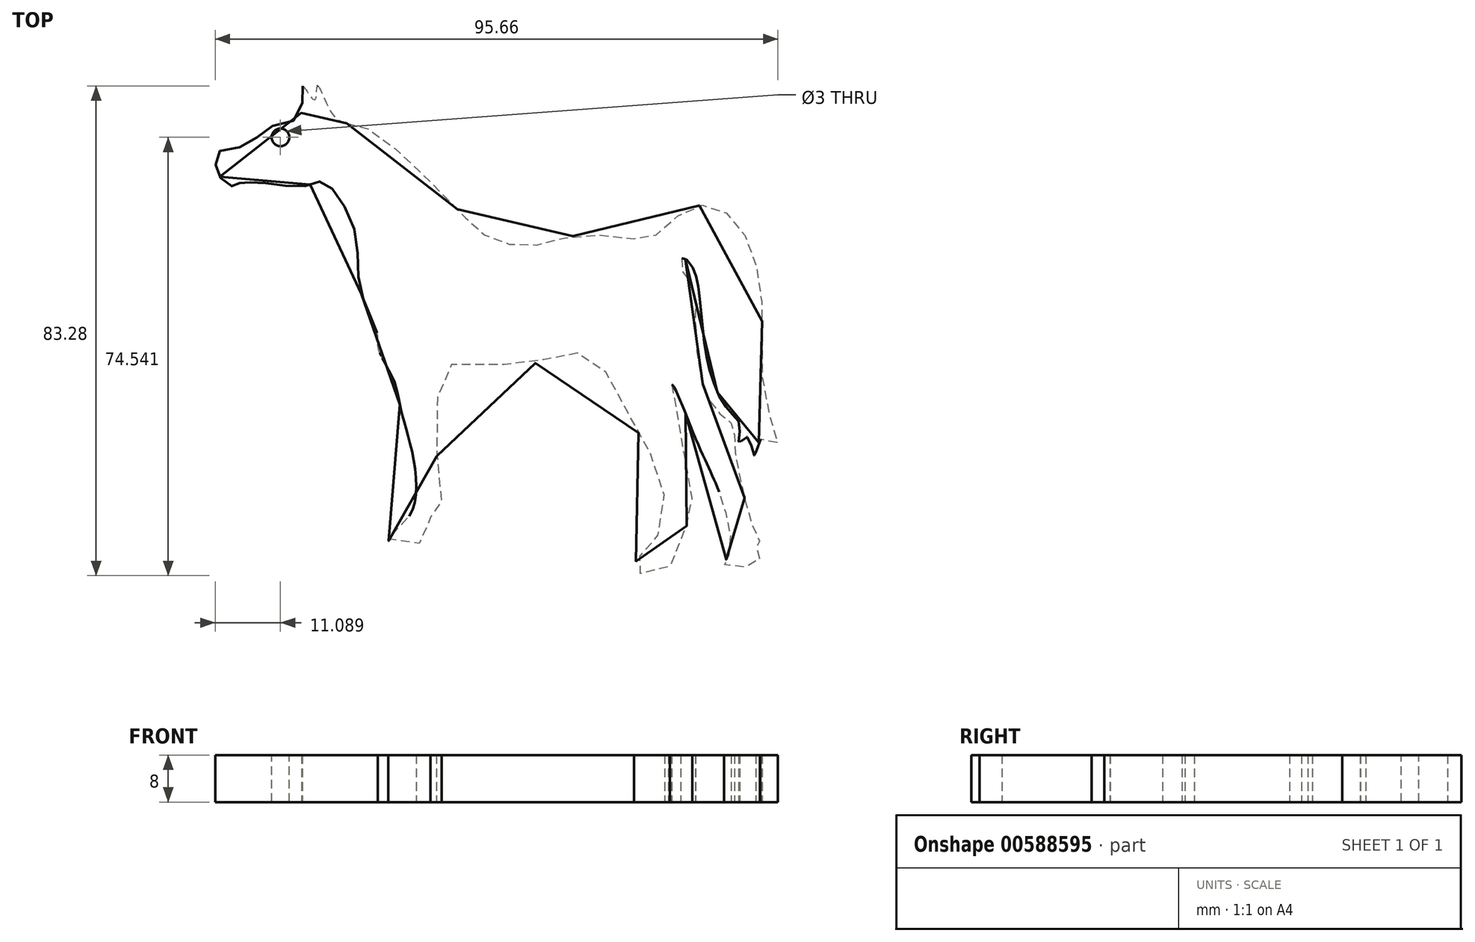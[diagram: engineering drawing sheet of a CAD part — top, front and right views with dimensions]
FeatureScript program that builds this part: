
annotation { "Feature Type Name" : "Feature", "Feature Type Description" : "" }
export const myFeature = defineFeature(function(context is Context, id is Id, definition is map)
    precondition{}
    {
        {
            var Q0;
            Q0=qCreatedBy(makeId("Top.planeOp"),FACE);
            var sketch = newSketch(context, id + "F0", { "sketchPlane" : qUnion([Q0])});
            skFitSpline(sketch, "E0", {"points": [v(-73.14, 76.23) * mm, v(-69.83, 75.44) * mm, v(-63.8, 70.88) * mm, v(-58.9, 66.2) * mm, v(-53.2, 60.4) * mm, v(-49.66, 57.2) * mm, v(-45.1, 55.6) * mm, v(-39.86, 55.72) * mm, v(-33.59, 57.2) * mm, v(-24.7, 56.63) * mm, v(-21.05, 56.97) * mm, v(-16.83, 60.5) * mm, v(-12.27, 62.33) * mm, v(-8.06, 60.5) * mm, v(-4.52, 55.15) * mm, v(-2.7, 46.94) * mm, v(-2.59, 37.03) * mm, v(-1.56, 27.45) * mm, v(0, 21.87) * mm, v(-2.47, 22.78) * mm, v(-3.84, 19.7) * mm, v(-5.1, 22.9) * mm, v(-6.46, 21.87) * mm, v(-6.35, 24.83) * mm, v(-8.29, 27.45) * mm, v(-11.25, 33.5) * mm, v(-12.62, 41.02) * mm, v(-13.41, 48.65) * mm, v(-14.67, 52.19) * mm, v(-16.15, 53.33) * mm, v(-15.92, 50.7) * mm, v(-14.33, 48.54) * mm, v(-13.87, 41.81) * mm, v(-12.39, 31.1) * mm, v(-9.65, 26.77) * mm, v(-7.49, 24.83) * mm, v(-7.26, 21.98) * mm, v(-6.12, 15.14) * mm, v(-3.73, 6.7) * mm, v(-2.93, 4.43) * mm, v(-3.61, 3.97) * mm, v(-3.04, 1.58) * mm, v(-8.86, 1.12) * mm, v(-8.29, 2.6) * mm, v(-8.17, 7.96) * mm, v(-10.45, 15.03) * mm, v(-13.76, 22.44) * mm, v(-17.86, 31.78) * mm, v(-15.24, 17.54) * mm, v(-14.9, 8.08) * mm, v(-15.8, 7.4) * mm, v(-16.26, 4.77) * mm, v(-18.43, 3.3) * mm, v(-18.43, 0) * mm, v(-23.9, 0) * mm, v(-24.13, 1.47) * mm, v(-22.42, 3.52) * mm, v(-20.02, 6.6) * mm, v(-19.45, 14.92) * mm, v(-23.33, 23.24) * mm, v(-28.23, 32.47) * mm, v(-32.33, 36.8) * mm, v(-38.37, 36.57) * mm, v(-43.05, 35.09) * mm, v(-55.59, 35.09) * mm, v(-57.75, 29.28) * mm, v(-57.52, 15.49) * mm, v(-57.4, 9.9) * mm, v(-58.78, 9.45) * mm, v(-59.46, 5.57) * mm, v(-65.84, 5) * mm, v(-65.73, 6.14) * mm, v(-62.08, 10.24) * mm, v(-62.08, 20.5) * mm, v(-64.02, 27.8) * mm, v(-65.16, 32.47) * mm, v(-67.78, 37.94) * mm, v(-67.9, 40.1) * mm, v(-69.03, 43.18) * mm, v(-71.09, 49.1) * mm, v(-71.54, 56.74) * mm, v(-74.62, 63.81) * mm, v(-77.47, 66.32) * mm, v(-80.43, 65.52) * mm, v(-85.9, 65.98) * mm, v(-89.55, 66.2) * mm, v(-91.26, 66.2) * mm, v(-91.94, 65.4) * mm, v(-94, 66.32) * mm, v(-95.12, 68.03) * mm, v(-95.12, 71.22) * mm, v(-90.23, 72.47) * mm, v(-86.13, 75.66) * mm, v(-81, 77.72) * mm, v(-80.66, 82.54) * mm, v(-78.6, 80.22) * mm, v(-78.15, 82.54) * mm, v(-75.76, 78.06) * mm, v(-73.14, 76.23) * mm]});
            skSolve(sketch);
        }
        {
            var Q0;
            Q0 = qSketchRegion(id + "F0", true);
            extrude(context, id + "F1", {"entities" : qUnion([Q0]), "depth" : 8 * mm, "offsetDistance" : 25 * mm});
        }
        {
            var Q0;
            Q0=makeQuery(id+"F1.opExtrude","CAP_FACE",FACE,{"disambiguationData":[OSD([sQuery(id+"F0.wireOp",EDGE,"E0")])],"isStart":false});
            var sketch = newSketch(context, id + "F2", { "sketchPlane" : qUnion([Q0])});
            skPoint(sketch, "E1", {"position": v(-84.42, 73.84) * mm});
            skSolve(sketch);
        }
        {
            var Q0;
            Q0=sQuery(id+"F2.wireOp",VERTEX,"E1");
            var Q1;
            Q1=makeQuery(id+"F1.opExtrude","SWEPT_BODY",BODY,{"disambiguationData":[OSD([sQuery(id+"F0.wireOp",EDGE,"E0")])]});
            hole(context, id + "F3", {"style" : HoleStyle.SIMPLE, "endStyle" : HoleEndStyle.THROUGH, "holeDiameter" : 3 * mm, "majorDiameter" : 5 * mm, "isTappedThrough" : true, "tappedDepth" : 12 * mm, "tapClearance" : 3, "locations" : qUnion([Q0]), "scope" : qUnion([Q1])});
        }
    });
